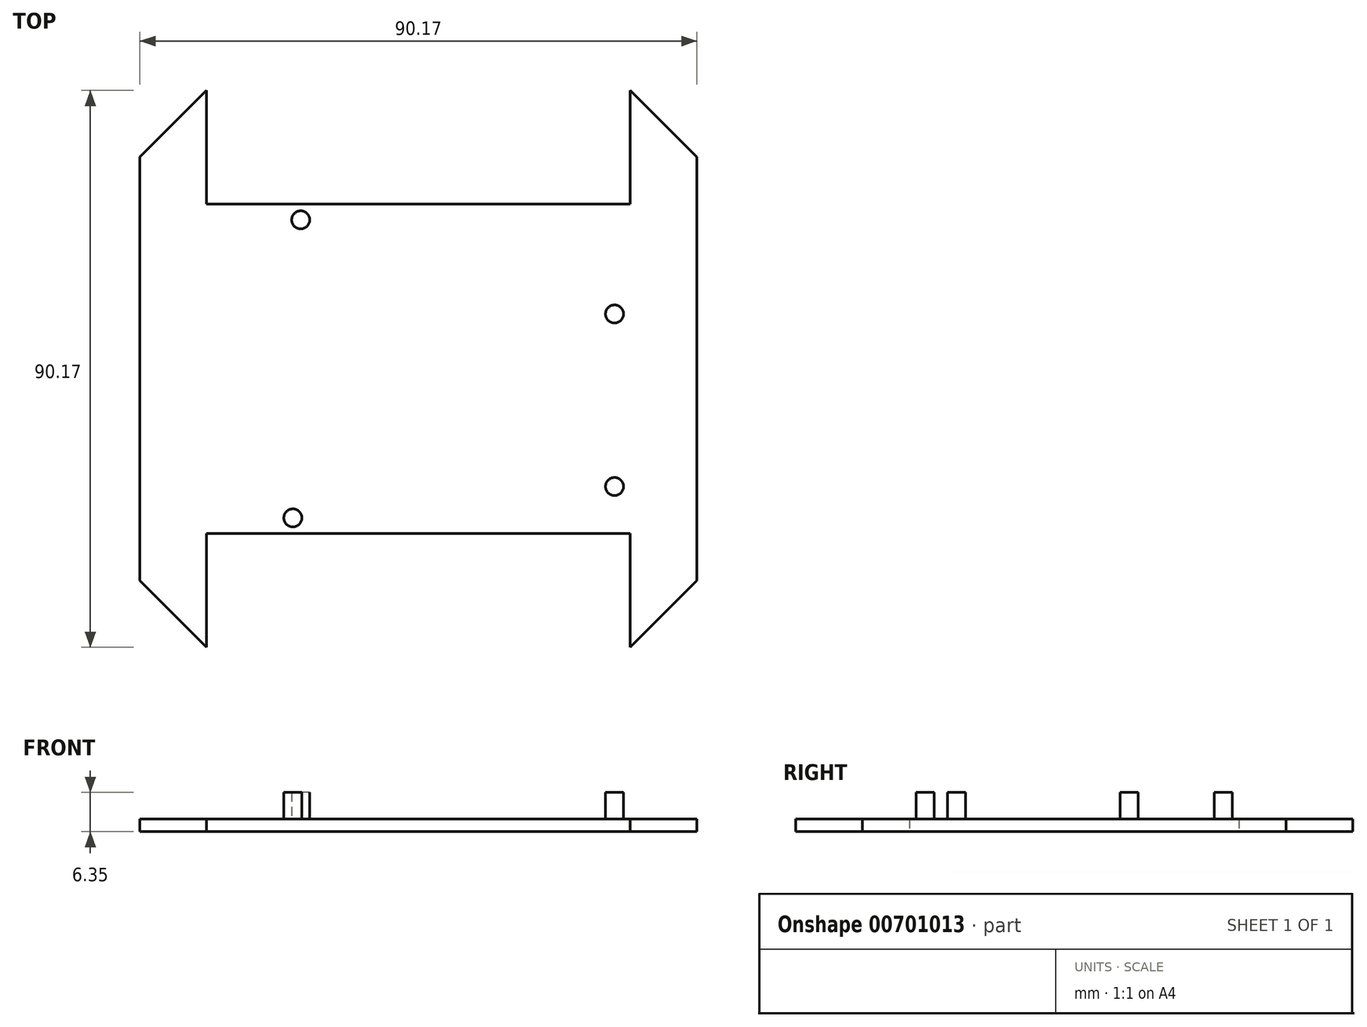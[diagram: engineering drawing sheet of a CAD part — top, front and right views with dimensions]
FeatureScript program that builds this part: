
annotation { "Feature Type Name" : "Feature", "Feature Type Description" : "" }
export const myFeature = defineFeature(function(context is Context, id is Id, definition is map)
    precondition{}
    {
        {
            var Q0;
            Q0=qCreatedBy(makeId("Top.planeOp"),FACE);
            var sketch = newSketch(context, id + "F0", { "sketchPlane" : qUnion([Q0])});
            skLineSegment(sketch, "E0.bottom", {"start": v(-51.17, -36.26) * mm, "end": v(39, -36.26) * mm});
            skLineSegment(sketch, "E0.top", {"start": v(-51.17, 55.18) * mm, "end": v(39, 55.18) * mm});
            skLineSegment(sketch, "E0.left", {"start": v(-51.17, -36.26) * mm, "end": v(-51.17, 55.18) * mm});
            skLineSegment(sketch, "E0.right", {"start": v(39, -36.26) * mm, "end": v(39, 55.18) * mm});
            skSolve(sketch);
        }
        {
            var Q0;
            Q0 = qSketchRegion(id + "F0", true);
            extrude(context, id + "F1", {"entities" : qUnion([Q0]), "depth" : 2.03 * mm, "offsetDistance" : 25.4 * mm});
        }
        {
            var Q0;
            Q0=makeQuery(id+"F1.opExtrude","SWEPT_EDGE",EDGE,{"disambiguationData":[OSD([sQuery(id+"F0.wireOp",EDGE,"E0.top"),sQuery(id+"F0.wireOp",EDGE,"E0.left")])]});
            var Q1;
            Q1=makeQuery(id+"F1.opExtrude","SWEPT_EDGE",EDGE,{"disambiguationData":[OSD([sQuery(id+"F0.wireOp",EDGE,"E0.bottom"),sQuery(id+"F0.wireOp",EDGE,"E0.left")])]});
            var Q2;
            Q2=makeQuery(id+"F1.opExtrude","SWEPT_EDGE",EDGE,{"disambiguationData":[OSD([sQuery(id+"F0.wireOp",EDGE,"E0.top"),sQuery(id+"F0.wireOp",EDGE,"E0.right")])]});
            var Q3;
            Q3=makeQuery(id+"F1.opExtrude","SWEPT_EDGE",EDGE,{"disambiguationData":[OSD([sQuery(id+"F0.wireOp",EDGE,"E0.bottom"),sQuery(id+"F0.wireOp",EDGE,"E0.right")])]});
            chamfer(context, id + "F2", {"entities" : qUnion([Q0, Q1, Q2, Q3]), "width" : 11.43 * mm, "tangentPropagation" : true});
        }
        {
            var Q0;
            Q0=qCreatedBy(makeId("Top.planeOp"),FACE);
            var sketch = newSketch(context, id + "F3", { "sketchPlane" : qUnion([Q0])});
            skLineSegment(sketch, "E1.bottom", {"start": v(-40.38, -37.53) * mm, "end": v(28.2, -37.53) * mm});
            skLineSegment(sketch, "E1.top", {"start": v(-40.38, -17.2) * mm, "end": v(28.2, -17.2) * mm});
            skLineSegment(sketch, "E1.left", {"start": v(-40.38, -37.53) * mm, "end": v(-40.38, -17.2) * mm});
            skLineSegment(sketch, "E1.right", {"start": v(28.2, -37.53) * mm, "end": v(28.2, -17.2) * mm});
            skLineSegment(sketch, "E2", {"start": v(-51.17, 9.46) * mm, "end": v(39, 9.46) * mm, "construction": true});
            skLineSegment(sketch, "E3", {"start": v(39, 43.75) * mm, "end": v(39, -24.83) * mm});
            skLineSegment(sketch, "E4.MirrorCS", {"start": v(-40.38, 36.13) * mm, "end": v(28.2, 36.13) * mm});
            skLineSegment(sketch, "E5.MirrorCS", {"start": v(-40.38, 56.45) * mm, "end": v(-40.38, 36.13) * mm});
            skLineSegment(sketch, "E6.MirrorCS", {"start": v(-40.38, 56.45) * mm, "end": v(28.2, 56.45) * mm});
            skLineSegment(sketch, "E7.MirrorCS", {"start": v(28.2, 56.45) * mm, "end": v(28.2, 36.13) * mm});
            skLineSegment(sketch, "E8", {"start": v(-6.09, 55.18) * mm, "end": v(-6.09, -36.26) * mm, "construction": true});
            skPoint(sketch, "E8.endSnap0", {"position": v(-6.09, 9.46) * mm});
            skLineSegment(sketch, "E9", {"start": v(28.2, 36.13) * mm, "end": v(28.2, -17.2) * mm, "construction": true});
            skSolve(sketch);
        }
        {
            var Q0;
            Q0 = qSketchRegion(id + "F3", true);
            extrude(context, id + "F4", {"entities" : qUnion([Q0]), "operationType" : NewBodyOperationType.REMOVE, "depth" : 25.4 * mm, "offsetDistance" : 25.4 * mm});
        }
        {
            var Q0;
            Q0=qCreatedBy(makeId("Top.planeOp"),FACE);
            var sketch = newSketch(context, id + "F5", { "sketchPlane" : qUnion([Q0])});
            skLineSegment(sketch, "E10", {"start": v(-40.38, 36.13) * mm, "end": v(-40.38, -17.2) * mm, "construction": true});
            skLineSegment(sketch, "E11", {"start": v(-26.4, 36.13) * mm, "end": v(-26.4, -17.2) * mm, "construction": true});
            skLineSegment(sketch, "E12", {"start": v(25.66, 36.13) * mm, "end": v(25.66, -17.2) * mm, "construction": true});
            skLineSegment(sketch, "E13", {"start": v(-25.14, 36.13) * mm, "end": v(-25.14, -17.2) * mm, "construction": true});
            skCircle(sketch, "E14", {"center": v(-26.4, -14.67) * mm, "radius": 1.46 * mm});
            skCircle(sketch, "E15", {"center": v(25.66, -9.59) * mm, "radius": 1.46 * mm});
            skCircle(sketch, "E16", {"center": v(25.66, 18.35) * mm, "radius": 1.46 * mm});
            skCircle(sketch, "E17", {"center": v(-25.14, 33.6) * mm, "radius": 1.46 * mm});
            skSolve(sketch);
        }
        {
            var Q0;
            Q0 = qSketchRegion(id + "F5", true);
            extrude(context, id + "F6", {"entities" : qUnion([Q0]), "operationType" : NewBodyOperationType.ADD, "depth" : 6.35 * mm, "offsetDistance" : 25.4 * mm});
        }
    });
